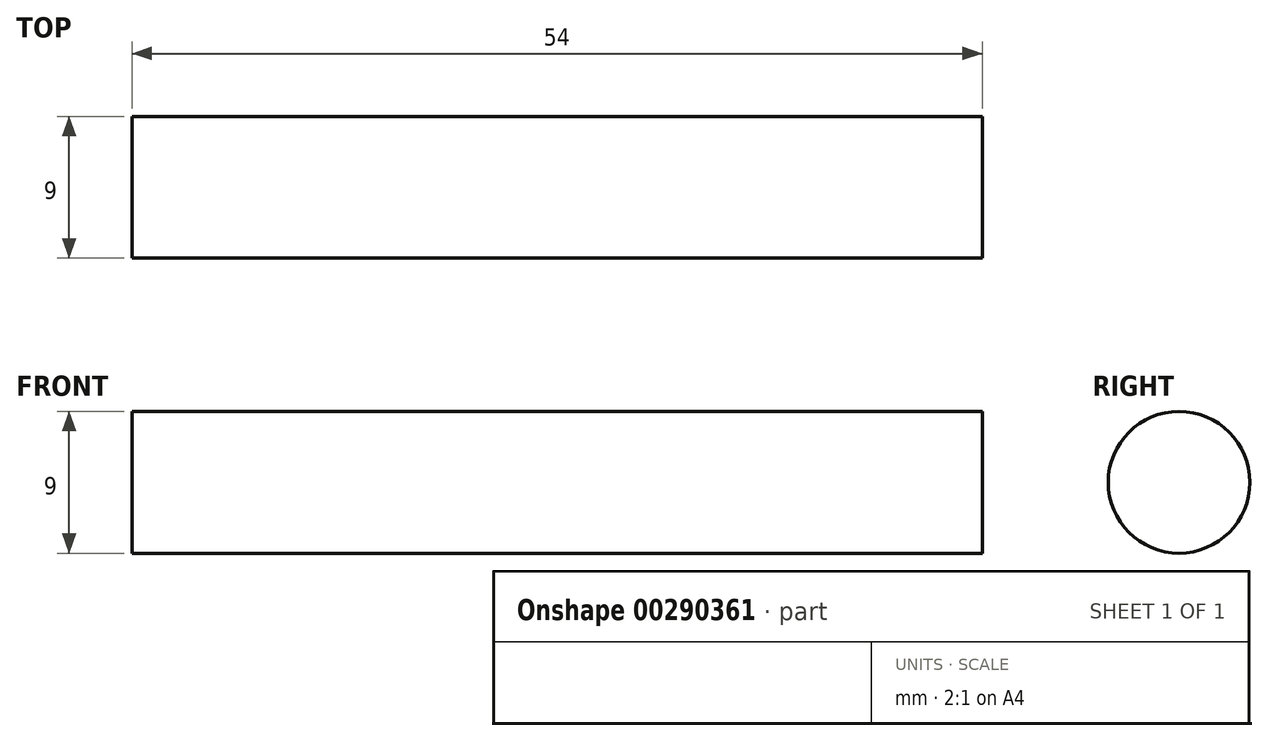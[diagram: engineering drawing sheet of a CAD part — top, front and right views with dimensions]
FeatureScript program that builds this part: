
annotation { "Feature Type Name" : "Feature", "Feature Type Description" : "" }
export const myFeature = defineFeature(function(context is Context, id is Id, definition is map)
    precondition{}
    {
        {
            var Q0;
            Q0=qCreatedBy(makeId("Front.planeOp"),FACE);
            var sketch = newSketch(context, id + "F0", { "sketchPlane" : qUnion([Q0])});
            skLineSegment(sketch, "E0", {"start": v(0, 4.5) * mm, "end": v(27, 4.5) * mm});
            skLineSegment(sketch, "E1", {"start": v(27, 4.5) * mm, "end": v(27, 0) * mm});
            skLineSegment(sketch, "E2.MirrorCS", {"start": v(0, 4.5) * mm, "end": v(-27, 4.5) * mm});
            skLineSegment(sketch, "E3.MirrorCS", {"start": v(-27, 4.5) * mm, "end": v(-27, 0) * mm});
            skLineSegment(sketch, "E4", {"start": v(27, 0) * mm, "end": v(-27, 0) * mm});
            skSolve(sketch);
        }
        {
            var Q0;
            Q0=makeQuery(id+"F0.imprint","IMPRINT",FACE,{"disambiguationData":[TD([[makeQuery(id+"F0.imprint","IMPRINT",EDGE,{"derivedFrom":sQuery(id+"F0.wireOp",EDGE,"E0")}),-1.0]])]});
            var Q1;
            Q1=sQuery(id+"F0.wireOp",EDGE,"E4");
            revolve(context, id + "F1", {"entities" : qUnion([Q0]), "axis" : qUnion([Q1]), "revolveType" : RevolveType.FULL});
        }
    });
